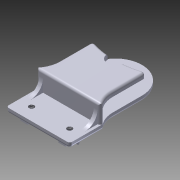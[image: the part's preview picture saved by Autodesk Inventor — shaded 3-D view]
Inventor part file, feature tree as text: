
AUTODESK INVENTOR PART (.ipt)
format: ipt  version: 2014 SP1 (Build 180222100, 222)  size: 372,736 bytes
history: native  units: mm
features: extrude x9, sketch x9, fillet x5, hole x1, chamfer x1, mirror x1
ambient origin geometry x8: Origin, YZ Plane, XZ Plane, XY Plane, X Axis, Y Axis, Z Axis, Center Point
bodies: Solid1 (feature_tree)
feature tree (26):
  extrude  "Extrusion1"  Depth=17.5mm
  sketch  "Sketch2"  dims[d3=6.35mm d4=10.5mm]
  extrude  "Extrusion2"  Depth=10.5mm
  extrude  "Extrusion3"  Depth=2.0mm
  extrude  "Extrusion4"  Depth=25.0mm
  sketch  "Sketch6"  dims[d12=1.0mm d13=0.0mm d14=2.0mm]
  hole  "Hole1"  [1 undecoded]
  extrude  "Extrusion5"  Depth=5.0mm
  extrude  "Extrusion6"  Depth=5.0mm
  extrude  "Extrusion7"  Depth=1.0mm TaperAngle=0.0deg
  chamfer  "Chamfer1"  Distance=1.0mm
  mirror  "Mirror1"
  fillet  "Fillet1"  Radius=1.0mm
  fillet  "Fillet2"  Radius=1.0mm
  fillet  "Fillet3"  Radius=1.0mm
  extrude  "Extrusion8"  Depth=10.5mm
  fillet  "Fillet4"  Radius=10.0mm
  extrude  "Extrusion9"  Depth=1.0mm
  fillet  "Fillet5"  Radius=1.5mm
  sketch  "Sketch1"  dims[d0=21.0mm d2=17.5mm]
  sketch  "Sketch3"  dims[d5=9.35mm d6=0.0mm d7=2.0mm]
  sketch  "Sketch4"  dims[d8=2.0mm d9=0.0mm d10=25.0mm]
  sketch  "Sketch7"  dims[d16=12.0mm d17=0.0mm d18=5.0mm]
  sketch  "Sketch8"  dims[d19=5.0mm d20=5.0mm]
  sketch  "Sketch9"  dims[d21=2.013mm d22=6.0mm d23=3.023mm d24=2.0mm d25=14.3117mm d26=8.0mm d27=20.594885mm d28=1.0mm d29=0.0mm]
  sketch  "Sketch10"  dims[d30=0.5mm d31=1.0mm d32=0.0mm d33=1.0mm d34=1.0mm d35=0.0mm d36=1.0mm d37=2.0mm d38=45.0deg d39=10.5mm d40=10.0mm d41=5.0mm d43=1.5mm d45=1.0mm d46=1.0mm d47=0.0mm d48=1.0mm d49=64.0mm d50=32.0mm d51=0.0mm d52=0.0mm d53=1.0mm]
note: 1 required parameter value undecoded (feature->parameter linkage not recoverable at this tier; creation-order binding heuristic only, values carry confidence <= 0.55)
